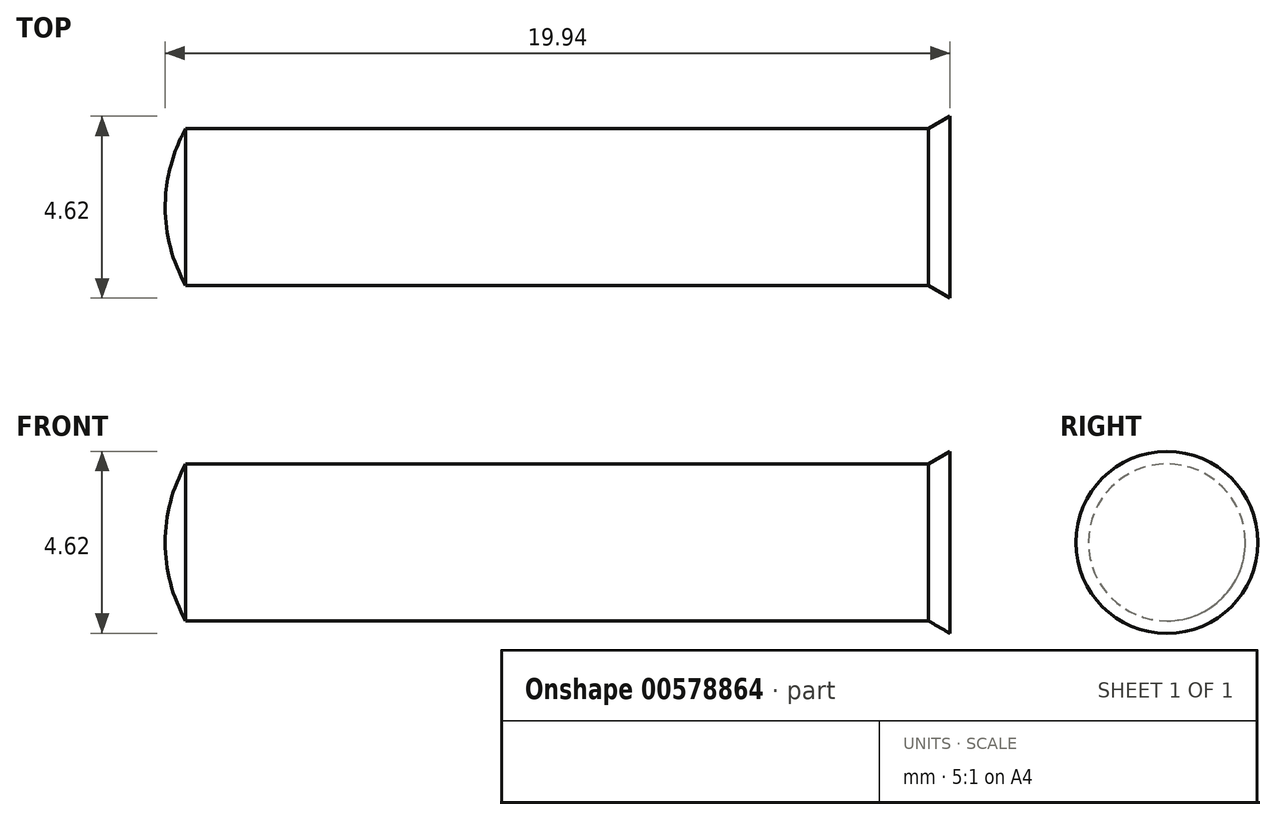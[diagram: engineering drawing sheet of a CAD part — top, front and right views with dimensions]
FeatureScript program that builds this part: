
annotation { "Feature Type Name" : "Feature", "Feature Type Description" : "" }
export const myFeature = defineFeature(function(context is Context, id is Id, definition is map)
    precondition{}
    {
        {
            var Q0;
            Q0=qCreatedBy(makeId("Right.planeOp"),FACE);
            var sketch = newSketch(context, id + "F0", { "sketchPlane" : qUnion([Q0])});
            skCircle(sketch, "E0", {"center": v(0, 0) * mm, "radius": 2 * mm});
            skSolve(sketch);
        }
        {
            var Q0;
            Q0=qSketchRegion(id+"F0",true);
            extrude(context, id + "F1", {"entities" : qUnion([Q0]), "oppositeDirection" : true, "depth" : 19.96 * mm});
        }
        {
            var Q0;
            Q0=qCreatedBy(makeId("Top.planeOp"),FACE);
            var sketch = newSketch(context, id + "F2", { "sketchPlane" : qUnion([Q0])});
            skLineSegment(sketch, "E1", {"start": v(-19.96, 2) * mm, "end": v(-0.55, 2) * mm});
            skLineSegment(sketch, "E2.0", {"start": v(0, 2) * mm, "end": v(0, -2) * mm});
            skLineSegment(sketch, "E3", {"start": v(0, 0) * mm, "end": v(-0.6, 0) * mm});
            skLineSegment(sketch, "E4", {"start": v(-0.6, 0) * mm, "end": v(-0.6, 2) * mm});
            skLineSegment(sketch, "E5", {"start": v(0, 2) * mm, "end": v(0, 2.31) * mm});
            skLineSegment(sketch, "E6", {"start": v(0, 2.31) * mm, "end": v(-0.55, 2) * mm});
            skSolve(sketch);
        }
        {
            var Q0;
            Q0=qSketchRegion(id+"F2",true);
            var Q1;
            Q1=sQuery(id+"F2.wireOp",EDGE,"E3");
            revolve(context, id + "F3", {"operationType" : NewBodyOperationType.ADD, "entities" : qUnion([Q0]), "axis" : qUnion([Q1]), "revolveType" : RevolveType.FULL});
        }
        {
            var Q0;
            Q0=qCreatedBy(makeId("Top.planeOp"),FACE);
            var sketch = newSketch(context, id + "F4", { "sketchPlane" : qUnion([Q0])});
            skPoint(sketch, "E7.orphan", {"position": v(-19.96, -2) * mm});
            skLineSegment(sketch, "E8.0", {"start": v(-19.96, 2) * mm, "end": v(-19.96, -2) * mm});
            skLineSegment(sketch, "E9", {"start": v(-19.96, 2) * mm, "end": v(-19.42, 2) * mm});
            skLineSegment(sketch, "E10", {"start": v(-19.42, -2) * mm, "end": v(-19.96, -2) * mm});
            skArc(sketch, "E11", {"start": v(-19.42, 2) * mm, "mid": v(-19.94, 0) * mm, "end": v(-19.42, -2) * mm});
            skLineSegment(sketch, "E12", {"start": v(-19.96, 0) * mm, "end": v(-19.94, 0) * mm});
            skSolve(sketch);
        }
        {
            var Q0;
            {var subQ2=sQuery(id+"F4.wireOp",EDGE,"E10");Q0=makeQuery(id+"F4.imprint","IMPRINT",FACE,{"disambiguationData":[TD([[makeQuery(id+"F4.imprint","IMPRINT",EDGE,{"derivedFrom":subQ2}),-1.0]])]});}
            var Q1;
            Q1=sQuery(id+"F4.wireOp",EDGE,"E12");
            revolve(context, id + "F5", {"operationType" : NewBodyOperationType.REMOVE, "entities" : qUnion([Q0]), "axis" : qUnion([Q1]), "revolveType" : RevolveType.FULL, "oppositeDirection" : true});
        }
    });
